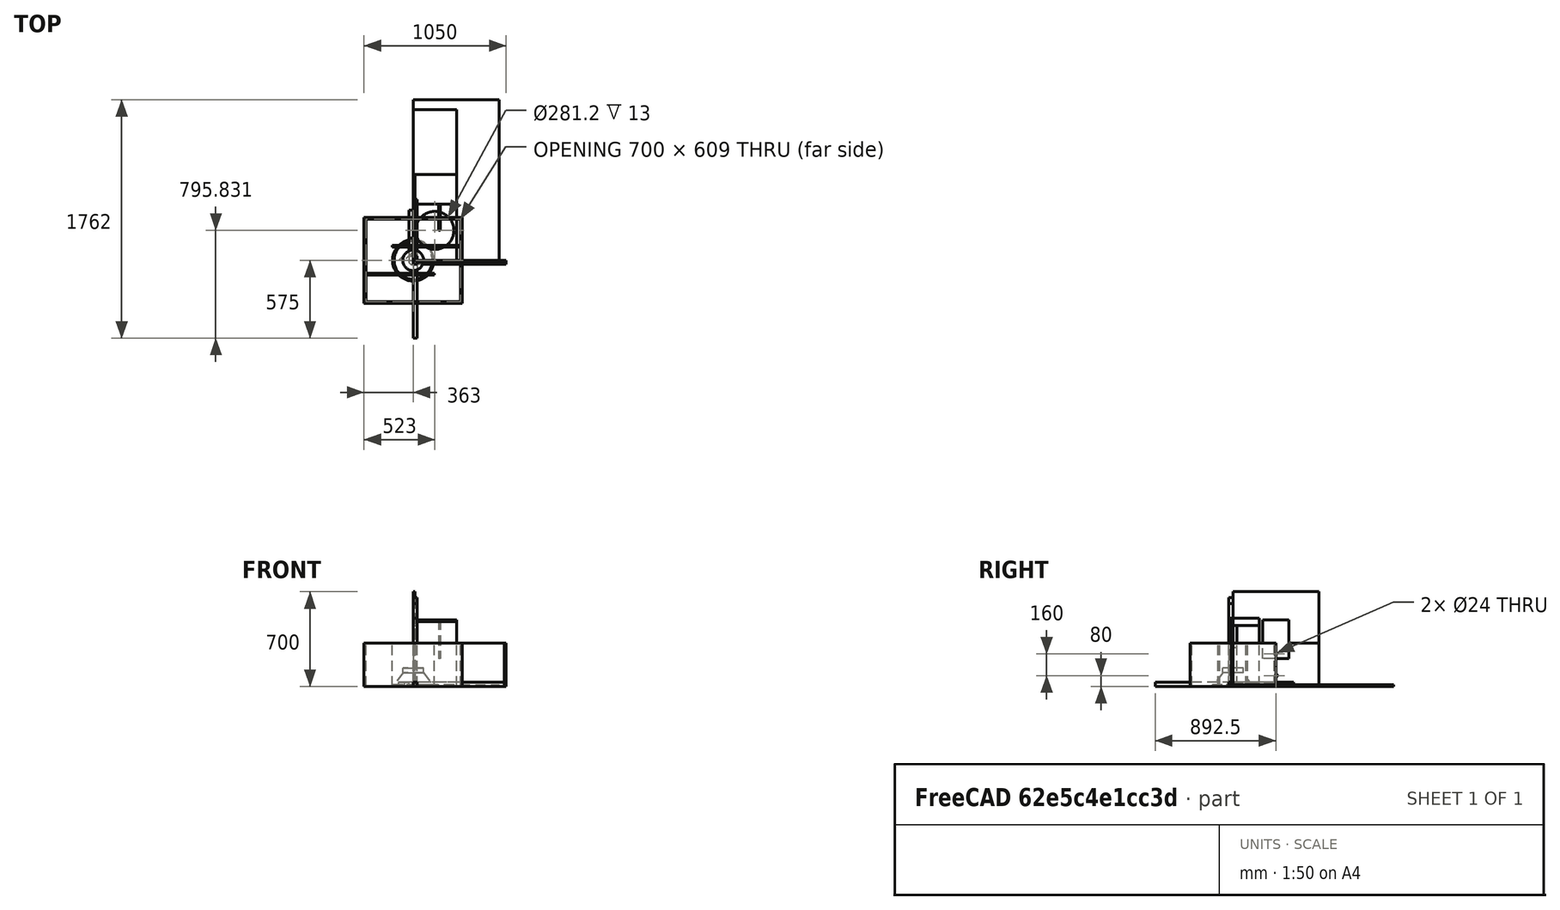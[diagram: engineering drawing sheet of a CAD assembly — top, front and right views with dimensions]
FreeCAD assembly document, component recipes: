
FREECAD ASSEMBLY — COMPONENT RECIPES ("gfold")

This assembly document has 41 components, labeled P0..P40 below (a component is one placed body or linked part). 41 of them carry a construction recipe — the FreeCAD feature program that regenerates the part from scratch, quoted from this document or its linked companion documents; the rest are supplied as boundary geometry only. No exploded tour is included for this assembly.
COMPONENT P0 — recipe-attached ("fin_support_1and2", modeled in this document).
Construction recipe (the document's own serialized feature program — sketch geometry with constraints, then the solid features built on it; lengths are millimeters unless a unit is written):

FEATURE [Sketcher::SketchObject] Sketch046
  ArcFitTolerance = 1e-06
  AttachmentSupport = -> [YZ_Plane037]
  FullyConstrained = true
  MakeInternals = false
  MapMode = 5
  Placement = pos=(0,0,0) rot=(0.57735,0.57735,0.57735;2.0944rad)
  expr: Constraints[10] = <<bdim>>.f12s_w
  expr: Constraints[9] = <<bdim>>.f12s_h
  sketch-geometry (4):
    g0: LineSegment StartX=0 StartY=0 StartZ=0 EndX=194.331 EndY=0 EndZ=0
    g1: LineSegment StartX=194.331 StartY=0 StartZ=0 EndX=194.331 EndY=285.337 EndZ=0
    g2: LineSegment StartX=194.331 StartY=285.337 StartZ=0 EndX=0 EndY=285.337 EndZ=0
    g3: LineSegment StartX=0 StartY=285.337 StartZ=0 EndX=0 EndY=0 EndZ=0
  constraints (11):
    c: Coincident(g0,g1)
    c: Coincident(g1,g2)
    c: Coincident(g2,g3)
    c: Coincident(g3,g0)
    c: Horizontal(g0)
    c: Horizontal(g2)
    c: Vertical(g1)
    c: Vertical(g3)
    c: Coincident(g0,g-1)
    c: DistanceX(g2,g2) = 194.331
    c: DistanceY(g1,g1) = 285.337
FEATURE [PartDesign::Pad] Pad034
  Direction = (1,0,0)
  Length = 13
  Length2 = 10
  Placement = pos=(0,0,0) rot=(1,1,1;2.0944rad)
  Profile = -> Sketch046
  ReferenceAxis = -> Sketch046 [N_Axis]
  Suppressed = false
  Type = 0
  expr: Length = <<bdim>>.f12s_t
FEATURE [PartDesign::Body] Body036  label="fin_support_1and2"
  AllowCompound = false
  Group = -> [Sketch046,Pad034]
  Origin = -> Origin037
  Placement = pos=(201,220.337,492.669) rot=(0,1,0;3.14159rad)
  Tip = -> Pad034
COMPONENT P1 — recipe-attached ("12lfa_driver001", modeled in this document).
Construction recipe (the document's own serialized feature program — sketch geometry with constraints, then the solid features built on it; lengths are millimeters unless a unit is written):

FEATURE [Sketcher::SketchObject] Sketch019
  ArcFitTolerance = 1e-06
  AttachmentSupport = -> [YZ_Plane009]
  FullyConstrained = true
  MakeInternals = false
  MapMode = 5
  Placement = pos=(0,0,0) rot=(0.57735,0.57735,0.57735;2.0944rad)
  expr: Constraints[18] = <<bdim>>.dr_d
  expr: Constraints[19] = <<bdim>>.dr_tdiam / 2
  expr: Constraints[20] = 6.4 mm
  expr: Constraints[22] = <<bdim>>.baffle_diameter / 2
  expr: Constraints[23] = <<bdim>>.dr_tdiam / 4
  expr: Constraints[24] = <<bdim>>.dr_d / 4
  expr: Constraints[25] = <<bdim>>.dr_d / 4
  sketch-geometry (9):
    g0: ArcOfCircle CenterX=0 CenterY=207.3 CenterZ=0 NormalX=0 NormalY=0 NormalZ=1 AngleXU=0 Radius=207.3 StartAngle=4.71239 EndAngle=4.87702
    g1: LineSegment StartX=33.975 StartY=2.80308 StartZ=0 EndX=146.4 EndY=0 EndZ=0
    g2: LineSegment StartX=146.4 StartY=0 StartZ=0 EndX=152.8 EndY=0 EndZ=0
    g3: LineSegment StartX=152.8 StartY=0 StartZ=0 EndX=152.8 EndY=12.2 EndZ=0
    g4: LineSegment StartX=152.8 StartY=12.2 StartZ=0 EndX=140.6 EndY=12.2 EndZ=0
    g5: LineSegment StartX=140.6 StartY=12.2 StartZ=0 EndX=76.4 EndY=101.925 EndZ=0
    g6: LineSegment StartX=76.4 StartY=101.925 StartZ=0 EndX=76.4 EndY=135.9 EndZ=0
    g7: LineSegment StartX=76.4 StartY=135.9 StartZ=0 EndX=0 EndY=135.9 EndZ=0
    g8: LineSegment StartX=0 StartY=135.9 StartZ=0 EndX=-3.81e-14 EndY=0 EndZ=0
  constraints (27):
    c: Coincident(g0,g-1)
    c: PointOnObject(g0,g-2)
    c: Coincident(g1,g0)
    c: PointOnObject(g1,g-1)
    c: Coincident(g1,g2)
    c: PointOnObject(g2,g-1)
    c: Coincident(g2,g3)
    c: Vertical(g3)
    c: Coincident(g3,g4)
    c: Horizontal(g4)
    c: Coincident(g4,g5)
    c: Coincident(g5,g6)
    c: Vertical(g6)
    c: Coincident(g6,g7)
    c: PointOnObject(g7,g-2)
    c: Horizontal(g7)
    c: Coincident(g7,g8)
    c: Coincident(g8,g0)
    c: DistanceY(g8,g8) = 135.9
    c: DistanceX(g0,g2) = 152.8
    c: DistanceX(g2,g2) = 6.4
    c: Radius(g0) = 207.3
    c: DistanceX(g0,g4) = 140.6
    c: DistanceX(g7,g7) = 76.4
    c: DistanceY(g6,g6) = 33.975
    c: DistanceX(g0,g0) = 33.975
    c: Equal(g3,g4)
FEATURE [PartDesign::Revolution] Revolution
  Angle = 360
  Angle2 = 60
  Axis = (0,0,1)
  Base = (0,0,0)
  Placement = pos=(0,0,0) rot=(1,1,1;2.0944rad)
  Profile = -> Sketch019
  ReferenceAxis = -> Sketch019 [V_Axis]
  Reversed = true
  Suppressed = false
  Type = 0
FEATURE [PartDesign::Body] Body008  label="12lfa_driver"
  AllowCompound = false
  Group = -> [Sketch019,Revolution]
  Origin = -> Origin009
  Tip = -> Revolution
COMPONENT P2 — recipe-attached ("back_panel001", modeled in this document).
Construction recipe (the document's own serialized feature program — sketch geometry with constraints, then the solid features built on it; lengths are millimeters unless a unit is written):

FEATURE [Sketcher::SketchObject] Sketch014
  ArcFitTolerance = 1e-06
  AttachmentSupport = -> [YZ_Plane004]
  FullyConstrained = true
  MakeInternals = false
  MapMode = 5
  Placement = pos=(0,0,0) rot=(0.57735,0.57735,0.57735;2.0944rad)
  expr: Constraints[10] = <<bdim>>.bp_w
  expr: Constraints[25] = <<bdim>>.bp_h * 0.25
  expr: Constraints[26] = <<bdim>>.spkon_bl
  expr: Constraints[28] = <<bdim>>.spkon_cd
  expr: Constraints[29] = <<bdim>>.bp_w / 2
  expr: Constraints[31] = <<bdim>>.bp_h * 0.25
  expr: Constraints[32] = <<bdim>>.bp_w / 2
  expr: Constraints[9] = <<bdim>>.bp_h
  sketch-geometry (13):
    g0: LineSegment StartX=0 StartY=0 StartZ=0 EndX=635 EndY=0 EndZ=0
    g1: LineSegment StartX=635 StartY=0 StartZ=0 EndX=635 EndY=320 EndZ=0
    g2: LineSegment StartX=635 StartY=320 StartZ=0 EndX=0 EndY=320 EndZ=0
    g3: LineSegment StartX=0 StartY=320 StartZ=0 EndX=0 EndY=0 EndZ=0
    g4: LineSegment [constr] StartX=332.1 StartY=254.6 StartZ=0 EndX=332.1 EndY=225.4 EndZ=0
    g5: LineSegment [constr] StartX=332.1 StartY=225.4 StartZ=0 EndX=302.9 EndY=225.4 EndZ=0
    g6: LineSegment [constr] StartX=302.9 StartY=225.4 StartZ=0 EndX=302.9 EndY=254.6 EndZ=0
    g7: LineSegment [constr] StartX=302.9 StartY=254.6 StartZ=0 EndX=332.1 EndY=254.6 EndZ=0
    g8: LineSegment [constr] StartX=332.1 StartY=225.4 StartZ=0 EndX=302.9 EndY=254.6 EndZ=0
    g9: LineSegment [constr] StartX=302.9 StartY=225.4 StartZ=0 EndX=332.1 EndY=254.6 EndZ=0
    g10: GeomPoint [constr] X=317.5 Y=240 Z=0
    g11: Circle CenterX=317.5 CenterY=240 CenterZ=0 NormalX=0 NormalY=0 NormalZ=1 AngleXU=0 Radius=12
    g12: Circle CenterX=317.5 CenterY=80 CenterZ=0 NormalX=0 NormalY=0 NormalZ=1 AngleXU=0 Radius=12
  constraints (33):
    c: Coincident(g0,g1)
    c: Coincident(g1,g2)
    c: Coincident(g2,g3)
    c: Coincident(g3,g0)
    c: Horizontal(g0)
    c: Horizontal(g2)
    c: Vertical(g1)
    c: Vertical(g3)
    c: Coincident(g0,g-1)
    c: DistanceY(g3,g3) = 320
    c: DistanceX(g0,g0) = 635
    c: Coincident(g4,g5)
    c: Coincident(g5,g6)
    c: Coincident(g6,g7)
    c: Coincident(g7,g4)
    c: Vertical(g4)
    c: Vertical(g6)
    c: Horizontal(g5)
    c: Horizontal(g7)
    c: Equal(g5,g4)
    c: Coincident(g8,g4)
    c: Coincident(g8,g6)
    c: Coincident(g9,g5)
    c: Coincident(g9,g4)
    c: Symmetric(g8,g8,g10)
    c: DistanceY(g10,g2) = 80
    c: DistanceY(g6,g6) = 29.2
    c: Coincident(g11,g10)
    c: Diameter(g11) = 24
    c: DistanceX(g2,g10) = 317.5
    c: Equal(g12,g11)
    c: DistanceY(g0,g12) = 80
    c: DistanceX(g0,g12) = 317.5
FEATURE [PartDesign::Pad] Pad003
  Direction = (1,0,0)
  Length = 13
  Length2 = 10
  Placement = pos=(0,0,0) rot=(1,1,1;2.0944rad)
  Profile = -> Sketch014
  ReferenceAxis = -> Sketch014 [N_Axis]
  Suppressed = false
  Type = 0
  expr: Length = <<bdim>>.bp_t
FEATURE [PartDesign::Body] Body003  label="back_panel"
  AllowCompound = false
  Group = -> [Sketch014,Pad003]
  Origin = -> Origin004
  Tip = -> Pad003
COMPONENT P3 — recipe-attached ("bottom_panel001", modeled in this document).
Construction recipe (the document's own serialized feature program — sketch geometry with constraints, then the solid features built on it; lengths are millimeters unless a unit is written):

FEATURE [Sketcher::SketchObject] Sketch017
  ArcFitTolerance = 1e-06
  AttachmentSupport = -> [YZ_Plane007]
  FullyConstrained = true
  MakeInternals = false
  MapMode = 5
  Placement = pos=(0,0,0) rot=(0.57735,0.57735,0.57735;2.0944rad)
  expr: Constraints[10] = <<bdim>>.tp_h
  expr: Constraints[9] = <<bdim>>.tp_w
  sketch-geometry (4):
    g0: LineSegment StartX=0 StartY=0 StartZ=0 EndX=635 EndY=0 EndZ=0
    g1: LineSegment StartX=635 StartY=0 StartZ=0 EndX=635 EndY=700 EndZ=0
    g2: LineSegment StartX=635 StartY=700 StartZ=0 EndX=0 EndY=700 EndZ=0
    g3: LineSegment StartX=0 StartY=700 StartZ=0 EndX=0 EndY=0 EndZ=0
  constraints (11):
    c: Coincident(g0,g1)
    c: Coincident(g1,g2)
    c: Coincident(g2,g3)
    c: Coincident(g3,g0)
    c: Horizontal(g0)
    c: Horizontal(g2)
    c: Vertical(g1)
    c: Vertical(g3)
    c: Coincident(g0,g-1)
    c: DistanceX(g0,g0) = 635
    c: DistanceY(g3,g3) = 700
FEATURE [PartDesign::Pad] Pad006
  Direction = (1,0,0)
  Length = 13
  Length2 = 10
  Placement = pos=(0,0,0) rot=(1,1,1;2.0944rad)
  Profile = -> Sketch017
  ReferenceAxis = -> Sketch017 [N_Axis]
  Suppressed = false
  Type = 0
  expr: Length = <<bdim>>.tp_t
FEATURE [PartDesign::Body] Body006  label="bottom_panel"
  AllowCompound = false
  Group = -> [Sketch017,Pad006]
  Origin = -> Origin007
  Tip = -> Pad006
COMPONENT P4 — recipe-attached ("brace_bar_back_panel_b", modeled in this document).
Construction recipe (the document's own serialized feature program — sketch geometry with constraints, then the solid features built on it; lengths are millimeters unless a unit is written):

FEATURE [Sketcher::SketchObject] Sketch037
  ArcFitTolerance = 1e-06
  AttachmentSupport = -> [XY_Plane027]
  FullyConstrained = true
  MakeInternals = false
  MapMode = 5
  expr: Constraints[10] = <<bdim>>.bbbp1_w
  expr: Constraints[9] = <<bdim>>.bbbp1_t
  sketch-geometry (4):
    g0: LineSegment StartX=0 StartY=0 StartZ=0 EndX=0 EndY=371.669 EndZ=0
    g1: LineSegment StartX=0 StartY=371.669 StartZ=0 EndX=-30 EndY=371.669 EndZ=0
    g2: LineSegment StartX=-30 StartY=371.669 StartZ=0 EndX=-30 EndY=0 EndZ=0
    g3: LineSegment StartX=-30 StartY=0 StartZ=0 EndX=0 EndY=0 EndZ=0
  constraints (11):
    c: Coincident(g0,g1)
    c: Coincident(g1,g2)
    c: Coincident(g2,g3)
    c: Coincident(g3,g0)
    c: Vertical(g0)
    c: Vertical(g2)
    c: Horizontal(g1)
    c: Horizontal(g3)
    c: Coincident(g0,g-1)
    c: DistanceX(g1,g1) = 30
    c: DistanceY(g2,g2) = 371.669
FEATURE [PartDesign::Pad] Pad025
  Direction = (0,0,1)
  Length = 30
  Length2 = 10
  Profile = -> Sketch037
  ReferenceAxis = -> Sketch037 [N_Axis]
  Suppressed = false
  Type = 0
  expr: Length = <<bdim>>.bbbp1_t
FEATURE [PartDesign::Body] Body026  label="brace_bar_back_panel_2"
  AllowCompound = false
  Group = -> [Sketch037,Pad025]
  Origin = -> Origin027
  Tip = -> Pad025
COMPONENT P5 — recipe-attached ("brace_bar_back_panel_c", modeled in this document).
Construction recipe (the document's own serialized feature program — sketch geometry with constraints, then the solid features built on it; lengths are millimeters unless a unit is written):

FEATURE [Sketcher::SketchObject] Sketch036
  ArcFitTolerance = 1e-06
  AttachmentSupport = -> [XY_Plane026]
  FullyConstrained = true
  MakeInternals = false
  MapMode = 5
  expr: Constraints[10] = <<bdim>>.bbbp2_w
  expr: Constraints[9] = <<bdim>>.bbbp2_t
  sketch-geometry (4):
    g0: LineSegment StartX=0 StartY=0 StartZ=0 EndX=0 EndY=164.331 EndZ=0
    g1: LineSegment StartX=0 StartY=164.331 StartZ=0 EndX=-30 EndY=164.331 EndZ=0
    g2: LineSegment StartX=-30 StartY=164.331 StartZ=0 EndX=-30 EndY=0 EndZ=0
    g3: LineSegment StartX=-30 StartY=0 StartZ=0 EndX=0 EndY=0 EndZ=0
  constraints (11):
    c: Coincident(g0,g1)
    c: Coincident(g1,g2)
    c: Coincident(g2,g3)
    c: Coincident(g3,g0)
    c: Vertical(g0)
    c: Vertical(g2)
    c: Horizontal(g1)
    c: Horizontal(g3)
    c: Coincident(g0,g-1)
    c: DistanceX(g1,g1) = 30
    c: DistanceY(g2,g2) = 164.331
FEATURE [PartDesign::Pad] Pad024
  Direction = (0,0,1)
  Length = 30
  Length2 = 10
  Profile = -> Sketch036
  ReferenceAxis = -> Sketch036 [N_Axis]
  Suppressed = false
  Type = 0
  expr: Length = <<bdim>>.bbbp1_t
FEATURE [PartDesign::Body] Body025  label="brace_bar_back_panel_1"
  AllowCompound = false
  Group = -> [Sketch036,Pad024]
  Origin = -> Origin026
  Tip = -> Pad024
COMPONENT P6 — same part as P4; its construction recipe is shown at P4.
COMPONENT P7 — same part as P5; its construction recipe is shown at P5.
COMPONENT P8 — same part as P4; its construction recipe is shown at P4.
COMPONENT P9 — recipe-attached ("brace bar fin 2 a", modeled in this document).
Construction recipe (the document's own serialized feature program — sketch geometry with constraints, then the solid features built on it; lengths are millimeters unless a unit is written):

FEATURE [Sketcher::SketchObject] Sketch034
  ArcFitTolerance = 1e-06
  AttachmentSupport = -> [YZ_Plane024]
  FullyConstrained = true
  MakeInternals = false
  MapMode = 5
  Placement = pos=(0,0,0) rot=(0.57735,0.57735,0.57735;2.0944rad)
  expr: Constraints[10] = <<bdim>>.bbf2_w
  expr: Constraints[9] = <<bdim>>.bbf2_h
  sketch-geometry (4):
    g0: LineSegment StartX=0 StartY=0 StartZ=0 EndX=30 EndY=0 EndZ=0
    g1: LineSegment StartX=30 StartY=0 StartZ=0 EndX=30 EndY=449.669 EndZ=0
    g2: LineSegment StartX=30 StartY=449.669 StartZ=0 EndX=0 EndY=449.669 EndZ=0
    g3: LineSegment StartX=0 StartY=449.669 StartZ=0 EndX=0 EndY=0 EndZ=0
  constraints (11):
    c: Coincident(g0,g1)
    c: Coincident(g1,g2)
    c: Coincident(g2,g3)
    c: Coincident(g3,g0)
    c: Horizontal(g0)
    c: Horizontal(g2)
    c: Vertical(g1)
    c: Vertical(g3)
    c: Coincident(g0,g-1)
    c: DistanceX(g2,g2) = 30
    c: DistanceY(g1,g1) = 449.669
FEATURE [PartDesign::Pad] Pad022
  Direction = (1,0,0)
  Length = 30
  Length2 = 10
  Placement = pos=(0,0,0) rot=(1,1,1;2.0944rad)
  Profile = -> Sketch034
  ReferenceAxis = -> Sketch034 [N_Axis]
  Suppressed = false
  Type = 0
  expr: Length = <<bdim>>.bbf2_t
FEATURE [PartDesign::Body] Body023  label="brace bar fin 2"
  AllowCompound = false
  Group = -> [Sketch034,Pad022]
  Origin = -> Origin024
  Tip = -> Pad022
COMPONENT P10 — recipe-attached ("brace bar fin 1 a", modeled in this document).
Construction recipe (the document's own serialized feature program — sketch geometry with constraints, then the solid features built on it; lengths are millimeters unless a unit is written):

FEATURE [Sketcher::SketchObject] Sketch035
  ArcFitTolerance = 1e-06
  AttachmentSupport = -> [YZ_Plane025]
  FullyConstrained = true
  MakeInternals = false
  MapMode = 5
  Placement = pos=(0,0,0) rot=(0.57735,0.57735,0.57735;2.0944rad)
  expr: Constraints[10] = <<bdim>>.bbf1_w
  expr: Constraints[9] = <<bdim>>.bbf2_h
  sketch-geometry (4):
    g0: LineSegment StartX=0 StartY=0 StartZ=0 EndX=30 EndY=0 EndZ=0
    g1: LineSegment StartX=30 StartY=0 StartZ=0 EndX=30 EndY=449.669 EndZ=0
    g2: LineSegment StartX=30 StartY=449.669 StartZ=0 EndX=0 EndY=449.669 EndZ=0
    g3: LineSegment StartX=0 StartY=449.669 StartZ=0 EndX=0 EndY=0 EndZ=0
  constraints (11):
    c: Coincident(g0,g1)
    c: Coincident(g1,g2)
    c: Coincident(g2,g3)
    c: Coincident(g3,g0)
    c: Horizontal(g0)
    c: Horizontal(g2)
    c: Vertical(g1)
    c: Vertical(g3)
    c: Coincident(g0,g-1)
    c: DistanceX(g2,g2) = 30
    c: DistanceY(g1,g1) = 449.669
FEATURE [PartDesign::Pad] Pad023
  Direction = (1,0,0)
  Length = 30
  Length2 = 10
  Placement = pos=(0,0,0) rot=(1,1,1;2.0944rad)
  Profile = -> Sketch035
  ReferenceAxis = -> Sketch035 [N_Axis]
  Suppressed = false
  Type = 0
  expr: Length = <<bdim>>.bbf2_t
FEATURE [PartDesign::Body] Body024  label="brace bar fin 1"
  AllowCompound = false
  Group = -> [Sketch035,Pad023]
  Origin = -> Origin025
  Tip = -> Pad023
COMPONENT P11 — same part as P10; its construction recipe is shown at P10.
COMPONENT P12 — same part as P9; its construction recipe is shown at P9.
COMPONENT P13 — recipe-attached ("driver_brace_bar_a", modeled in this document).
Construction recipe (the document's own serialized feature program — sketch geometry with constraints, then the solid features built on it; lengths are millimeters unless a unit is written):

FEATURE [Sketcher::SketchObject] Sketch038
  ArcFitTolerance = 1e-06
  AttachmentSupport = -> [XY_Plane029]
  FullyConstrained = true
  MakeInternals = false
  MapMode = 5
  expr: Constraints[12] = <<bdim>>.dbb_h
  expr: Constraints[13] = <<bdim>>.dbb_w
  sketch-geometry (5):
    g0: LineSegment StartX=0 StartY=106.066 StartZ=0 EndX=0 EndY=63.6396 EndZ=0
    g1: LineSegment StartX=0 StartY=63.6396 StartZ=0 EndX=-63.6396 EndY=0 EndZ=0
    g2: LineSegment StartX=-63.6396 StartY=0 StartZ=0 EndX=-106.066 EndY=0 EndZ=0
    g3: LineSegment StartX=-106.066 StartY=0 StartZ=0 EndX=0 EndY=106.066 EndZ=0
    g4: LineSegment [constr] StartX=-84.8528 StartY=21.2132 StartZ=0 EndX=-63.6396 EndY=0 EndZ=0
  constraints (15):
    c: PointOnObject(g0,g-2)
    c: PointOnObject(g0,g-2)
    c: Coincident(g0,g1)
    c: PointOnObject(g1,g-1)
    c: Coincident(g1,g2)
    c: PointOnObject(g2,g-1)
    c: Coincident(g2,g3)
    c: Coincident(g3,g0)
    c: Equal(g0,g2)
    c: Parallel(g3,g1)
    c: PointOnObject(g4,g3)
    c: Perpendicular(g3,g4)
    c: Distance(g4) = 30
    c: Distance(g3) = 150
    c: Coincident(g4,g1)
FEATURE [PartDesign::Pad] Pad027
  Direction = (0,0,1)
  Length = 30
  Length2 = 10
  Profile = -> Sketch038
  ReferenceAxis = -> Sketch038 [N_Axis]
  Suppressed = false
  Type = 0
  expr: Length = <<bdim>>.dbb_t
FEATURE [PartDesign::Body] Body028  label="driver_brace_bar"
  AllowCompound = false
  Group = -> [Sketch038,Pad027]
  Origin = -> Origin029
  Tip = -> Pad027
COMPONENT P14 — same part as P13; its construction recipe is shown at P13.
COMPONENT P15 — recipe-attached ("fin_1", modeled in this document).
Construction recipe (the document's own serialized feature program — sketch geometry with constraints, then the solid features built on it; lengths are millimeters unless a unit is written):

FEATURE [Sketcher::SketchObject] Sketch030
  ArcFitTolerance = 1e-06
  AttachmentSupport = -> [XZ_Plane020]
  FullyConstrained = true
  MakeInternals = false
  MapMode = 5
  Placement = pos=(0,0,0) rot=(1,0,0;1.5708rad)
  expr: Constraints[10] = <<bdim>>.f1_h
  expr: Constraints[9] = <<bdim>>.f1_w
  sketch-geometry (4):
    g0: LineSegment StartX=0 StartY=0 StartZ=0 EndX=320 EndY=0 EndZ=0
    g1: LineSegment StartX=320 StartY=0 StartZ=0 EndX=320 EndY=479.669 EndZ=0
    g2: LineSegment StartX=320 StartY=479.669 StartZ=0 EndX=0 EndY=479.669 EndZ=0
    g3: LineSegment StartX=0 StartY=479.669 StartZ=0 EndX=0 EndY=0 EndZ=0
  constraints (11):
    c: Coincident(g0,g1)
    c: Coincident(g1,g2)
    c: Coincident(g2,g3)
    c: Coincident(g3,g0)
    c: Horizontal(g0)
    c: Horizontal(g2)
    c: Vertical(g1)
    c: Vertical(g3)
    c: Coincident(g0,g-1)
    c: DistanceY(g1,g1) = 479.669
    c: DistanceX(g0,g0) = 320
FEATURE [PartDesign::Pad] Pad018
  Direction = (0,-1,2e-16)
  Length = 13
  Length2 = 10
  Placement = pos=(0,0,0) rot=(1,0,0;1.5708rad)
  Profile = -> Sketch030
  ReferenceAxis = -> Sketch030 [N_Axis]
  Suppressed = false
  Type = 0
  expr: Length = <<bdim>>.f1_t
FEATURE [PartDesign::Body] Body019  label="fin_1_model"
  AllowCompound = false
  Group = -> [Sketch030,Pad018]
  Origin = -> Origin020
  Tip = -> Pad018
COMPONENT P16 — recipe-attached ("fin 1 support001", modeled in this document).
Construction recipe (the document's own serialized feature program — sketch geometry with constraints, then the solid features built on it; lengths are millimeters unless a unit is written):

FEATURE [Sketcher::SketchObject] Sketch042
  ArcFitTolerance = 1e-06
  AttachmentSupport = -> [YZ_Plane033]
  FullyConstrained = true
  MakeInternals = false
  MapMode = 5
  Placement = pos=(0,0,0) rot=(0.57735,0.57735,0.57735;2.0944rad)
  expr: Constraints[10] = <<bdim>>.f2s_w
  expr: Constraints[9] = <<bdim>>.f2s_h
  sketch-geometry (4):
    g0: LineSegment StartX=0 StartY=0 StartZ=0 EndX=194.331 EndY=0 EndZ=0
    g1: LineSegment StartX=194.331 StartY=0 StartZ=0 EndX=194.331 EndY=505.669 EndZ=0
    g2: LineSegment StartX=194.331 StartY=505.669 StartZ=0 EndX=0 EndY=505.669 EndZ=0
    g3: LineSegment StartX=0 StartY=505.669 StartZ=0 EndX=0 EndY=0 EndZ=0
  constraints (11):
    c: Coincident(g0,g1)
    c: Coincident(g1,g2)
    c: Coincident(g2,g3)
    c: Coincident(g3,g0)
    c: Horizontal(g0)
    c: Horizontal(g2)
    c: Vertical(g1)
    c: Vertical(g3)
    c: Coincident(g0,g-1)
    c: DistanceX(g2,g2) = 194.331
    c: DistanceY(g3,g3) = 505.669
FEATURE [PartDesign::Pad] Pad030
  Direction = (1,0,0)
  Length = 13
  Length2 = 10
  Placement = pos=(0,0,0) rot=(1,1,1;2.0944rad)
  Profile = -> Sketch042
  ReferenceAxis = -> Sketch042 [N_Axis]
  Suppressed = false
  Type = 0
  expr: Length = <<bdim>>.f2s_t
FEATURE [PartDesign::Body] Body032  label="fin 2 support"
  AllowCompound = false
  Group = -> [Sketch042,Pad030]
  Origin = -> Origin033
  Tip = -> Pad030
COMPONENT P17 — recipe-attached ("fin 1 support002", modeled in this document).
Construction recipe (the document's own serialized feature program — sketch geometry with constraints, then the solid features built on it; lengths are millimeters unless a unit is written):

FEATURE [Sketcher::SketchObject] Sketch043
  ArcFitTolerance = 1e-06
  AttachmentSupport = -> [YZ_Plane034]
  FullyConstrained = true
  MakeInternals = false
  MapMode = 5
  Placement = pos=(0,0,0) rot=(0.57735,0.57735,0.57735;2.0944rad)
  expr: Constraints[10] = <<bdim>>.f1s_w
  expr: Constraints[9] = <<bdim>>.f1s_h
  sketch-geometry (4):
    g0: LineSegment StartX=0 StartY=0 StartZ=0 EndX=194.331 EndY=0 EndZ=0
    g1: LineSegment StartX=194.331 StartY=0 StartZ=0 EndX=194.331 EndY=449.669 EndZ=0
    g2: LineSegment StartX=194.331 StartY=449.669 StartZ=0 EndX=0 EndY=449.669 EndZ=0
    g3: LineSegment StartX=0 StartY=449.669 StartZ=0 EndX=0 EndY=0 EndZ=0
  constraints (11):
    c: Coincident(g0,g1)
    c: Coincident(g1,g2)
    c: Coincident(g2,g3)
    c: Coincident(g3,g0)
    c: Horizontal(g0)
    c: Horizontal(g2)
    c: Vertical(g1)
    c: Vertical(g3)
    c: Coincident(g0,g-1)
    c: DistanceX(g2,g2) = 194.331
    c: DistanceY(g3,g3) = 449.669
FEATURE [PartDesign::Pad] Pad031
  Direction = (1,0,0)
  Length = 13
  Length2 = 10
  Placement = pos=(0,0,0) rot=(1,1,1;2.0944rad)
  Profile = -> Sketch043
  ReferenceAxis = -> Sketch043 [N_Axis]
  Suppressed = false
  Type = 0
  expr: Length = <<bdim>>.f1s_t
FEATURE [PartDesign::Body] Body033  label="fin 1 support"
  AllowCompound = false
  Group = -> [Sketch043,Pad031]
  Origin = -> Origin034
  Tip = -> Pad031
COMPONENT P18 — recipe-attached ("fin_2", modeled in this document).
Construction recipe (the document's own serialized feature program — sketch geometry with constraints, then the solid features built on it; lengths are millimeters unless a unit is written):

FEATURE [Sketcher::SketchObject] Sketch031
  ArcFitTolerance = 1e-06
  AttachmentSupport = -> [XZ_Plane021]
  FullyConstrained = true
  MakeInternals = false
  MapMode = 5
  Placement = pos=(0,0,0) rot=(1,0,0;1.5708rad)
  expr: Constraints[10] = <<bdim>>.f2_h
  expr: Constraints[9] = <<bdim>>.f2_w
  sketch-geometry (4):
    g0: LineSegment StartX=0 StartY=0 StartZ=0 EndX=320 EndY=0 EndZ=0
    g1: LineSegment StartX=320 StartY=0 StartZ=0 EndX=320 EndY=492.669 EndZ=0
    g2: LineSegment StartX=320 StartY=492.669 StartZ=0 EndX=0 EndY=492.669 EndZ=0
    g3: LineSegment StartX=0 StartY=492.669 StartZ=0 EndX=0 EndY=0 EndZ=0
  constraints (11):
    c: Coincident(g0,g1)
    c: Coincident(g1,g2)
    c: Coincident(g2,g3)
    c: Coincident(g3,g0)
    c: Horizontal(g0)
    c: Horizontal(g2)
    c: Vertical(g1)
    c: Vertical(g3)
    c: Coincident(g0,g-1)
    c: DistanceY(g1,g1) = 492.669
    c: DistanceX(g0,g0) = 320
FEATURE [PartDesign::Pad] Pad019
  Direction = (0,-1,2e-16)
  Length = 13
  Length2 = 10
  Placement = pos=(0,0,0) rot=(1,0,0;1.5708rad)
  Profile = -> Sketch031
  ReferenceAxis = -> Sketch031 [N_Axis]
  Suppressed = false
  Type = 0
  expr: Length = <<bdim>>.f2_t
FEATURE [PartDesign::Body] Body020  label="fin_2_model"
  AllowCompound = false
  Group = -> [Sketch031,Pad019]
  Origin = -> Origin021
  Tip = -> Pad019
COMPONENT P19 — recipe-attached ("front_panel_bar_b", modeled in this document).
Construction recipe (the document's own serialized feature program — sketch geometry with constraints, then the solid features built on it; lengths are millimeters unless a unit is written):

FEATURE [Sketcher::SketchObject] Sketch033
  ArcFitTolerance = 1e-06
  AttachmentSupport = -> [XY_Plane023]
  FullyConstrained = true
  MakeInternals = false
  MapMode = 5
  expr: Constraints[13] = <<bdim>>.fpb_h
  expr: Constraints[15] = (<<bdim>>.baffle_diameter + <<bdim>>.dr_tdiam) / 4
  expr: Constraints[16] = <<bdim>>.fp_h / 2
  expr: Constraints[17] = <<dims>>.width1 + <<bdim>>.sp_thick * 0.5 + <<dims>>.driver_offset - <<bdim>>.bar_side_size - <<bdim>>.sp_thick
  expr: Constraints[6] = <<bdim>>.fpb_t
  sketch-geometry (6):
    g0: LineSegment StartX=0 StartY=0 StartZ=0 EndX=30 EndY=0 EndZ=0
    g1: LineSegment StartX=30 StartY=371.663 StartZ=0 EndX=0 EndY=371.663 EndZ=0
    g2: LineSegment StartX=0 StartY=371.663 StartZ=0 EndX=0 EndY=0 EndZ=0
    g3: LineSegment StartX=30 StartY=371.663 StartZ=0 EndX=30 EndY=261.809 EndZ=0
    g4: LineSegment StartX=30 StartY=0 StartZ=0 EndX=30 EndY=125.854 EndZ=0
    g5: ArcOfCircle CenterX=160 CenterY=193.831 CenterZ=0 NormalX=0 NormalY=0 NormalZ=1 AngleXU=0 Radius=146.7 StartAngle=2.65979 EndAngle=3.62339
  constraints (18):
    c: Coincident(g1,g2)
    c: Coincident(g2,g0)
    c: Horizontal(g0)
    c: Horizontal(g1)
    c: Vertical(g2)
    c: Coincident(g0,g-1)
    c: DistanceX(g1,g1) = 30
    c: Coincident(g3,g1)
    c: Vertical(g3)
    c: Coincident(g4,g0)
    c: Vertical(g4)
    c: Coincident(g5,g3)
    c: Coincident(g5,g4)
    c: DistanceY(g2,g2) = 371.663
    c: Equal(g1,g0)
    c: Radius(g5) = 146.7
    c: DistanceX(g0,g5) = 160
    c: DistanceY(g5,g1) = 177.831
FEATURE [PartDesign::Pad] Pad021
  Direction = (0,0,1)
  Length = 30
  Length2 = 10
  Profile = -> Sketch033
  ReferenceAxis = -> Sketch033 [N_Axis]
  Suppressed = false
  Type = 0
  expr: Length = <<bdim>>.bar_side_size
FEATURE [PartDesign::Body] Body022  label="fp_bar_1"
  AllowCompound = false
  Group = -> [Sketch033,Pad021]
  Origin = -> Origin023
  Tip = -> Pad021
COMPONENT P20 — same part as P19; its construction recipe is shown at P19.
COMPONENT P21 — recipe-attached ("front_panel001", modeled in this document).
Construction recipe (the document's own serialized feature program — sketch geometry with constraints, then the solid features built on it; lengths are millimeters unless a unit is written):

FEATURE [Sketcher::SketchObject] Sketch032
  ArcFitTolerance = 1e-06
  AttachmentSupport = -> [XY_Plane022]
  FullyConstrained = true
  MakeInternals = false
  MapMode = 5
  expr: Constraints[10] = <<bdim>>.fp_w
  expr: Constraints[18] = <<bdim>>.baffle_diameter
  expr: Constraints[19] = <<dims>>.width1 + <<bdim>>.sp_thick * 0.5 + <<dims>>.driver_offset
  expr: Constraints[9] = <<bdim>>.fp_h
  sketch-geometry (7):
    g0: LineSegment StartX=0 StartY=0 StartZ=0 EndX=320 EndY=0 EndZ=0
    g1: LineSegment StartX=320 StartY=0 StartZ=0 EndX=320 EndY=414.663 EndZ=0
    g2: LineSegment StartX=320 StartY=414.663 StartZ=0 EndX=0 EndY=414.663 EndZ=0
    g3: LineSegment StartX=0 StartY=414.663 StartZ=0 EndX=0 EndY=0 EndZ=0
    g4: Circle CenterX=160 CenterY=220.831 CenterZ=0 NormalX=0 NormalY=0 NormalZ=1 AngleXU=0 Radius=140.6
    g5: LineSegment [constr] StartX=0 StartY=220.831 StartZ=0 EndX=160 EndY=220.831 EndZ=0
    g6: LineSegment [constr] StartX=160 StartY=220.831 StartZ=0 EndX=320 EndY=220.831 EndZ=0
  constraints (20):
    c: Coincident(g0,g1)
    c: Coincident(g1,g2)
    c: Coincident(g2,g3)
    c: Coincident(g3,g0)
    c: Horizontal(g0)
    c: Horizontal(g2)
    c: Vertical(g1)
    c: Vertical(g3)
    c: Coincident(g0,g-1)
    c: DistanceX(g2,g2) = 320
    c: DistanceY(g3,g3) = 414.663
    c: PointOnObject(g5,g3)
    c: Coincident(g5,g4)
    c: Horizontal(g5)
    c: Coincident(g6,g4)
    c: PointOnObject(g6,g1)
    c: Parallel(g6,g5)
    c: Equal(g5,g6)
    c: Diameter(g4) = 281.2
    c: DistanceY(g0,g5) = 220.831
FEATURE [PartDesign::Pad] Pad020
  Direction = (0,0,1)
  Length = 13
  Length2 = 10
  Profile = -> Sketch032
  ReferenceAxis = -> Sketch032 [N_Axis]
  Suppressed = false
  Type = 0
  expr: Length = <<bdim>>.fp_t
FEATURE [PartDesign::Body] Body021  label="front_panel"
  AllowCompound = false
  Group = -> [Sketch032,Pad020]
  Origin = -> Origin022
  Tip = -> Pad020
COMPONENT P22 — recipe-attached ("brace_bar_back_panel_e", modeled in this document).
Construction recipe (the document's own serialized feature program — sketch geometry with constraints, then the solid features built on it; lengths are millimeters unless a unit is written):

FEATURE [Sketcher::SketchObject] Sketch050
  ArcFitTolerance = 1e-06
  AttachmentSupport = -> [XY_Plane041]
  FullyConstrained = true
  MakeInternals = false
  MapMode = 5
  expr: Constraints[10] = <<bdim>>.mbbbp2_h
  expr: Constraints[9] = <<bdim>>.mbbbp2_w
  sketch-geometry (4):
    g0: LineSegment StartX=0 StartY=0 StartZ=0 EndX=30 EndY=0 EndZ=0
    g1: LineSegment StartX=30 StartY=0 StartZ=0 EndX=30 EndY=134.331 EndZ=0
    g2: LineSegment StartX=30 StartY=134.331 StartZ=0 EndX=0 EndY=134.331 EndZ=0
    g3: LineSegment StartX=0 StartY=134.331 StartZ=0 EndX=0 EndY=0 EndZ=0
  constraints (11):
    c: Coincident(g0,g1)
    c: Coincident(g1,g2)
    c: Coincident(g2,g3)
    c: Coincident(g3,g0)
    c: Horizontal(g0)
    c: Horizontal(g2)
    c: Vertical(g1)
    c: Vertical(g3)
    c: Coincident(g0,g-1)
    c: DistanceY(g3,g3) = 134.331
    c: DistanceX(g2,g2) = 30
FEATURE [PartDesign::Pad] Pad038
  Direction = (0,0,1)
  Length = 30
  Length2 = 10
  Profile = -> Sketch050
  ReferenceAxis = -> Sketch050 [N_Axis]
  Suppressed = false
  Type = 0
  expr: Length = <<bdim>>.mbbbp2_t
FEATURE [PartDesign::Body] Body040  label="middle_brace_bar_back_panel_2_model"
  AllowCompound = false
  Group = -> [Sketch050,Pad038]
  Origin = -> Origin041
  Tip = -> Pad038
COMPONENT P23 — recipe-attached ("middle brace bar fin 1", modeled in this document).
Construction recipe (the document's own serialized feature program — sketch geometry with constraints, then the solid features built on it; lengths are millimeters unless a unit is written):

FEATURE [Sketcher::SketchObject] Sketch
  ArcFitTolerance = 1e-06
  AttachmentSupport = -> [YZ_Plane028]
  FullyConstrained = true
  MakeInternals = false
  MapMode = 5
  Placement = pos=(0,0,0) rot=(0.57735,0.57735,0.57735;2.0944rad)
  expr: Constraints[10] = <<bdim>>.mbbf1_w
  expr: Constraints[9] = <<bdim>>.mbbf1_h
  sketch-geometry (4):
    g0: LineSegment StartX=0 StartY=0 StartZ=0 EndX=449.669 EndY=0 EndZ=0
    g1: LineSegment StartX=449.669 StartY=0 StartZ=0 EndX=449.669 EndY=30 EndZ=0
    g2: LineSegment StartX=449.669 StartY=30 StartZ=0 EndX=0 EndY=30 EndZ=0
    g3: LineSegment StartX=0 StartY=30 StartZ=0 EndX=0 EndY=0 EndZ=0
  constraints (11):
    c: Coincident(g0,g1)
    c: Coincident(g1,g2)
    c: Coincident(g2,g3)
    c: Coincident(g3,g0)
    c: Horizontal(g0)
    c: Horizontal(g2)
    c: Vertical(g1)
    c: Vertical(g3)
    c: Coincident(g0,g-1)
    c: DistanceY(g1,g1) = 30
    c: DistanceX(g2,g2) = 449.669
FEATURE [PartDesign::Pad] Pad026
  Direction = (1,0,0)
  Length = 30
  Length2 = 10
  Placement = pos=(0,0,0) rot=(1,1,1;2.0944rad)
  Profile = -> Sketch
  ReferenceAxis = -> Sketch [N_Axis]
  Suppressed = false
  Type = 0
  expr: Length = <<bdim>>.mbbf1_t
FEATURE [PartDesign::Body] Body027  label="middle brace bar fin 1 model"
  AllowCompound = false
  Group = -> [Sketch,Pad026]
  Origin = -> Origin028
  Tip = -> Pad026
COMPONENT P24 — recipe-attached ("middle_brace_bar_fin_1and_2_fin2", modeled in this document).
Construction recipe (the document's own serialized feature program — sketch geometry with constraints, then the solid features built on it; lengths are millimeters unless a unit is written):

FEATURE [Sketcher::SketchObject] Sketch045
  ArcFitTolerance = 1e-06
  AttachmentSupport = -> [YZ_Plane036]
  FullyConstrained = true
  MakeInternals = false
  MapMode = 5
  Placement = pos=(0,0,0) rot=(0.57735,0.57735,0.57735;2.0944rad)
  expr: Constraints[10] = <<bdim>>.mbbf12_w
  expr: Constraints[9] = <<bdim>>.mbbf12_h
  sketch-geometry (4):
    g0: LineSegment StartX=0 StartY=0 StartZ=0 EndX=30 EndY=0 EndZ=0
    g1: LineSegment StartX=30 StartY=0 StartZ=0 EndX=30 EndY=285.337 EndZ=0
    g2: LineSegment StartX=30 StartY=285.337 StartZ=0 EndX=0 EndY=285.337 EndZ=0
    g3: LineSegment StartX=0 StartY=285.337 StartZ=0 EndX=0 EndY=0 EndZ=0
  constraints (11):
    c: Coincident(g0,g1)
    c: Coincident(g1,g2)
    c: Coincident(g2,g3)
    c: Coincident(g3,g0)
    c: Horizontal(g0)
    c: Horizontal(g2)
    c: Vertical(g1)
    c: Vertical(g3)
    c: Coincident(g0,g-1)
    c: DistanceX(g2,g2) = 30
    c: DistanceY(g1,g1) = 285.337
FEATURE [PartDesign::Pad] Pad033
  Direction = (1,0,0)
  Length = 30
  Length2 = 10
  Placement = pos=(0,0,0) rot=(1,1,1;2.0944rad)
  Profile = -> Sketch045
  ReferenceAxis = -> Sketch045 [N_Axis]
  Suppressed = false
  Type = 0
  expr: Length = <<bdim>>.mbbf12_t
FEATURE [PartDesign::Body] Body035  label="middle_brace_bar_fin_1and_2"
  AllowCompound = false
  Group = -> [Sketch045,Pad033]
  Origin = -> Origin036
  Tip = -> Pad033
COMPONENT P25 — same part as P24; its construction recipe is shown at P24.
COMPONENT P26 — recipe-attached ("middle_brace_bar_fin_2", modeled in this document).
Construction recipe (the document's own serialized feature program — sketch geometry with constraints, then the solid features built on it; lengths are millimeters unless a unit is written):

FEATURE [Sketcher::SketchObject] Sketch040
  ArcFitTolerance = 1e-06
  AttachmentSupport = -> [XZ_Plane031]
  FullyConstrained = true
  MakeInternals = false
  MapMode = 5
  Placement = pos=(0,0,0) rot=(1,0,0;1.5708rad)
  expr: Constraints[10] = <<bdim>>.mbbf2_w
  expr: Constraints[9] = <<bdim>>.mbbf2_h
  sketch-geometry (4):
    g0: LineSegment StartX=0 StartY=0 StartZ=0 EndX=30 EndY=0 EndZ=0
    g1: LineSegment StartX=30 StartY=0 StartZ=0 EndX=30 EndY=505.669 EndZ=0
    g2: LineSegment StartX=30 StartY=505.669 StartZ=0 EndX=0 EndY=505.669 EndZ=0
    g3: LineSegment StartX=0 StartY=505.669 StartZ=0 EndX=0 EndY=0 EndZ=0
  constraints (11):
    c: Coincident(g0,g1)
    c: Coincident(g1,g2)
    c: Coincident(g2,g3)
    c: Coincident(g3,g0)
    c: Horizontal(g0)
    c: Horizontal(g2)
    c: Vertical(g1)
    c: Vertical(g3)
    c: Coincident(g0,g-1)
    c: DistanceX(g2,g2) = 30
    c: DistanceY(g1,g1) = 505.669
FEATURE [PartDesign::Pad] Pad028
  Direction = (0,-1,2e-16)
  Length = 30
  Length2 = 10
  Placement = pos=(0,0,0) rot=(1,0,0;1.5708rad)
  Profile = -> Sketch040
  ReferenceAxis = -> Sketch040 [N_Axis]
  Suppressed = false
  Type = 0
  expr: Length = <<bdim>>.mbbf2_t
FEATURE [PartDesign::Body] Body030  label="middle_brace_bar_fin_2_model"
  AllowCompound = false
  Group = -> [Sketch040,Pad028]
  Origin = -> Origin031
  Tip = -> Pad028
COMPONENT P27 — recipe-attached ("middle_brace_bar_side_panel_1", modeled in this document).
Construction recipe (the document's own serialized feature program — sketch geometry with constraints, then the solid features built on it; lengths are millimeters unless a unit is written):

FEATURE [Sketcher::SketchObject] Sketch044
  ArcFitTolerance = 1e-06
  AttachmentSupport = -> [XZ_Plane035]
  FullyConstrained = true
  MakeInternals = false
  MapMode = 5
  Placement = pos=(0,0,0) rot=(1,0,0;1.5708rad)
  expr: Constraints[10] = <<bdim>>.mbbsp1_w
  expr: Constraints[9] = <<bdim>>.mbbsp1_h
  sketch-geometry (4):
    g0: LineSegment StartX=0 StartY=0 StartZ=0 EndX=30 EndY=0 EndZ=0
    g1: LineSegment StartX=30 StartY=0 StartZ=0 EndX=30 EndY=614 EndZ=0
    g2: LineSegment StartX=30 StartY=614 StartZ=0 EndX=0 EndY=614 EndZ=0
    g3: LineSegment StartX=0 StartY=614 StartZ=0 EndX=0 EndY=0 EndZ=0
  constraints (11):
    c: Coincident(g0,g1)
    c: Coincident(g1,g2)
    c: Coincident(g2,g3)
    c: Coincident(g3,g0)
    c: Horizontal(g0)
    c: Horizontal(g2)
    c: Vertical(g1)
    c: Vertical(g3)
    c: Coincident(g0,g-1)
    c: DistanceX(g2,g2) = 30
    c: DistanceY(g1,g1) = 614
FEATURE [PartDesign::Pad] Pad032
  AlongSketchNormal = false
  Direction = (0,-1,2e-16)
  Length = 30
  Length2 = 10
  Placement = pos=(0,0,0) rot=(1,0,0;1.5708rad)
  Profile = -> Sketch044
  ReferenceAxis = -> Sketch044 [N_Axis]
  Suppressed = false
  Type = 0
  expr: Length = <<bdim>>.mbbsp1_t
FEATURE [PartDesign::Body] Body034  label="middle_brace_bar_side_panel_1_model"
  AllowCompound = false
  Group = -> [Sketch044,Pad032]
  Origin = -> Origin035
  Tip = -> Pad032
COMPONENT P28 — recipe-attached ("middle_brace_bar_side_panel_2", modeled in this document).
Construction recipe (the document's own serialized feature program — sketch geometry with constraints, then the solid features built on it; lengths are millimeters unless a unit is written):

FEATURE [Sketcher::SketchObject] Sketch041
  ArcFitTolerance = 1e-06
  AttachmentSupport = -> [XZ_Plane032]
  FullyConstrained = true
  MakeInternals = false
  MapMode = 5
  Placement = pos=(0,0,0) rot=(1,0,0;1.5708rad)
  expr: Constraints[10] = <<bdim>>.mbbsp2_w
  expr: Constraints[9] = <<bdim>>.mbbsp2_h
  sketch-geometry (4):
    g0: LineSegment StartX=0 StartY=0 StartZ=0 EndX=30 EndY=0 EndZ=0
    g1: LineSegment StartX=30 StartY=0 StartZ=0 EndX=30 EndY=657 EndZ=0
    g2: LineSegment StartX=30 StartY=657 StartZ=0 EndX=0 EndY=657 EndZ=0
    g3: LineSegment StartX=0 StartY=657 StartZ=0 EndX=0 EndY=0 EndZ=0
  constraints (11):
    c: Coincident(g0,g1)
    c: Coincident(g1,g2)
    c: Coincident(g2,g3)
    c: Coincident(g3,g0)
    c: Horizontal(g0)
    c: Horizontal(g2)
    c: Vertical(g1)
    c: Vertical(g3)
    c: Coincident(g0,g-1)
    c: DistanceX(g2,g2) = 30
    c: DistanceY(g1,g1) = 657
FEATURE [PartDesign::Pad] Pad029
  Direction = (0,-1,2e-16)
  Length = 30
  Length2 = 10
  Placement = pos=(0,0,0) rot=(1,0,0;1.5708rad)
  Profile = -> Sketch041
  ReferenceAxis = -> Sketch041 [N_Axis]
  Suppressed = false
  Type = 0
  expr: Length = <<bdim>>.mbbsp2_t
FEATURE [PartDesign::Body] Body031  label="middle_brace_bar_side_panel_003"
  AllowCompound = false
  Group = -> [Sketch041,Pad029]
  Origin = -> Origin032
  Tip = -> Pad029
COMPONENT P29 — recipe-attached ("side_panel_1", modeled in this document).
Construction recipe (the document's own serialized feature program — sketch geometry with constraints, then the solid features built on it; lengths are millimeters unless a unit is written):

FEATURE [Sketcher::SketchObject] Sketch020
  ArcFitTolerance = 1e-06
  AttachmentSupport = -> [XZ_Plane010]
  FullyConstrained = true
  MakeInternals = false
  MapMode = 5
  Placement = pos=(0,0,0) rot=(1,0,0;1.5708rad)
  expr: Constraints[10] = <<bdim>>.sp_h
  expr: Constraints[9] = <<bdim>>.sp_w
  sketch-geometry (4):
    g0: LineSegment StartX=0 StartY=0 StartZ=0 EndX=674 EndY=0 EndZ=0
    g1: LineSegment StartX=674 StartY=0 StartZ=0 EndX=674 EndY=320 EndZ=0
    g2: LineSegment StartX=674 StartY=320 StartZ=0 EndX=0 EndY=320 EndZ=0
    g3: LineSegment StartX=0 StartY=320 StartZ=0 EndX=0 EndY=0 EndZ=0
  constraints (11):
    c: Coincident(g0,g1)
    c: Coincident(g1,g2)
    c: Coincident(g2,g3)
    c: Coincident(g3,g0)
    c: Horizontal(g0)
    c: Horizontal(g2)
    c: Vertical(g1)
    c: Vertical(g3)
    c: Coincident(g0,g-1)
    c: DistanceY(g3,g3) = 320
    c: DistanceX(g0,g0) = 674
FEATURE [PartDesign::Pad] Pad008
  Direction = (0,-1,2e-16)
  Length = 13
  Length2 = 10
  Placement = pos=(0,0,0) rot=(1,0,0;1.5708rad)
  Profile = -> Sketch020
  ReferenceAxis = -> Sketch020 [N_Axis]
  Suppressed = false
  Type = 0
  expr: Length = <<bdim>>.sp_thick
FEATURE [PartDesign::Body] Body009  label="side_panel_001"
  AllowCompound = false
  Group = -> [Sketch020,Pad008]
  Origin = -> Origin010
  Tip = -> Pad008
COMPONENT P30 — recipe-attached ("side_panel_1_bar_a", modeled in this document).
Construction recipe (the document's own serialized feature program — sketch geometry with constraints, then the solid features built on it; lengths are millimeters unless a unit is written):

FEATURE [Sketcher::SketchObject] Sketch021
  ArcFitTolerance = 1e-06
  AttachmentSupport = -> [XZ_Plane011]
  FullyConstrained = true
  MakeInternals = false
  MapMode = 5
  Placement = pos=(0,0,0) rot=(1,0,0;1.5708rad)
  expr: Constraints[10] = <<bdim>>.spb_h
  expr: Constraints[9] = <<bdim>>.spb_w
  sketch-geometry (4):
    g0: LineSegment StartX=0 StartY=0 StartZ=0 EndX=674 EndY=0 EndZ=0
    g1: LineSegment StartX=674 StartY=0 StartZ=0 EndX=674 EndY=30 EndZ=0
    g2: LineSegment StartX=674 StartY=30 StartZ=0 EndX=0 EndY=30 EndZ=0
    g3: LineSegment StartX=0 StartY=30 StartZ=0 EndX=0 EndY=0 EndZ=0
  constraints (11):
    c: Coincident(g0,g1)
    c: Coincident(g1,g2)
    c: Coincident(g2,g3)
    c: Coincident(g3,g0)
    c: Horizontal(g0)
    c: Horizontal(g2)
    c: Vertical(g1)
    c: Vertical(g3)
    c: Coincident(g0,g-1)
    c: DistanceX(g2,g2) = 674
    c: DistanceY(g3,g3) = 30
FEATURE [PartDesign::Pad] Pad009
  Direction = (0,-1,2e-16)
  Length = 30
  Length2 = 10
  Placement = pos=(0,0,0) rot=(1,0,0;1.5708rad)
  Profile = -> Sketch021
  ReferenceAxis = -> Sketch021 [N_Axis]
  Suppressed = false
  Type = 0
  expr: Length = <<bdim>>.spb_h
FEATURE [PartDesign::Body] Body010  label="side_panel_001_bar_001"
  AllowCompound = false
  Group = -> [Sketch021,Pad009]
  Origin = -> Origin011
  Tip = -> Pad009
COMPONENT P31 — recipe-attached ("side_panel_1_bar_b", modeled in this document).
Construction recipe (the document's own serialized feature program — sketch geometry with constraints, then the solid features built on it; lengths are millimeters unless a unit is written):

FEATURE [Sketcher::SketchObject] Sketch022
  ArcFitTolerance = 1e-06
  AttachmentSupport = -> [XZ_Plane012]
  FullyConstrained = true
  MakeInternals = false
  MapMode = 5
  Placement = pos=(0,0,0) rot=(1,0,0;1.5708rad)
  expr: Constraints[10] = <<bdim>>.spb_h
  expr: Constraints[9] = <<bdim>>.spb_w
  sketch-geometry (4):
    g0: LineSegment StartX=0 StartY=0 StartZ=0 EndX=674 EndY=0 EndZ=0
    g1: LineSegment StartX=674 StartY=0 StartZ=0 EndX=674 EndY=30 EndZ=0
    g2: LineSegment StartX=674 StartY=30 StartZ=0 EndX=0 EndY=30 EndZ=0
    g3: LineSegment StartX=0 StartY=30 StartZ=0 EndX=0 EndY=0 EndZ=0
  constraints (11):
    c: Coincident(g0,g1)
    c: Coincident(g1,g2)
    c: Coincident(g2,g3)
    c: Coincident(g3,g0)
    c: Horizontal(g0)
    c: Horizontal(g2)
    c: Vertical(g1)
    c: Vertical(g3)
    c: Coincident(g0,g-1)
    c: DistanceX(g2,g2) = 674
    c: DistanceY(g3,g3) = 30
FEATURE [PartDesign::Pad] Pad010
  Direction = (0,-1,2e-16)
  Length = 30
  Length2 = 10
  Placement = pos=(0,0,0) rot=(1,0,0;1.5708rad)
  Profile = -> Sketch022
  ReferenceAxis = -> Sketch022 [N_Axis]
  Suppressed = false
  Type = 0
  expr: Length = <<bdim>>.spb_h
FEATURE [PartDesign::Body] Body011  label="side_panel_001_bar_002"
  AllowCompound = false
  Group = -> [Sketch022,Pad010]
  Origin = -> Origin012
  Tip = -> Pad010
COMPONENT P32 — recipe-attached ("side_panel_1_bar_c", modeled in this document).
Construction recipe (the document's own serialized feature program — sketch geometry with constraints, then the solid features built on it; lengths are millimeters unless a unit is written):

FEATURE [Sketcher::SketchObject] Sketch023
  ArcFitTolerance = 1e-06
  AttachmentSupport = -> [XZ_Plane013]
  FullyConstrained = true
  MakeInternals = false
  MapMode = 5
  Placement = pos=(0,0,0) rot=(1,0,0;1.5708rad)
  expr: Constraints[10] = <<bdim>>.spbb_w
  expr: Constraints[9] = <<bdim>>.spbb_h
  sketch-geometry (4):
    g0: LineSegment StartX=0 StartY=0 StartZ=0 EndX=30 EndY=0 EndZ=0
    g1: LineSegment StartX=30 StartY=0 StartZ=0 EndX=30 EndY=260 EndZ=0
    g2: LineSegment StartX=30 StartY=260 StartZ=0 EndX=0 EndY=260 EndZ=0
    g3: LineSegment StartX=0 StartY=260 StartZ=0 EndX=0 EndY=0 EndZ=0
  constraints (11):
    c: Coincident(g0,g1)
    c: Coincident(g1,g2)
    c: Coincident(g2,g3)
    c: Coincident(g3,g0)
    c: Horizontal(g0)
    c: Horizontal(g2)
    c: Vertical(g1)
    c: Vertical(g3)
    c: Coincident(g0,g-1)
    c: DistanceX(g2,g2) = 30
    c: DistanceY(g3,g3) = 260
FEATURE [PartDesign::Pad] Pad011
  Direction = (0,-1,2e-16)
  Length = 30
  Length2 = 10
  Placement = pos=(0,0,0) rot=(1,0,0;1.5708rad)
  Profile = -> Sketch023
  ReferenceAxis = -> Sketch023 [N_Axis]
  Suppressed = false
  Type = 0
  expr: Length = <<bdim>>.spb_h
FEATURE [PartDesign::Body] Body012  label="side_panel_001_bar_003"
  AllowCompound = false
  Group = -> [Sketch023,Pad011]
  Origin = -> Origin013
  Tip = -> Pad011
COMPONENT P33 — recipe-attached ("side_panel_1_bar_d", modeled in this document).
Construction recipe (the document's own serialized feature program — sketch geometry with constraints, then the solid features built on it; lengths are millimeters unless a unit is written):

FEATURE [Sketcher::SketchObject] Sketch024
  ArcFitTolerance = 1e-06
  AttachmentSupport = -> [XZ_Plane014]
  FullyConstrained = true
  MakeInternals = false
  MapMode = 5
  Placement = pos=(0,0,0) rot=(1,0,0;1.5708rad)
  expr: Constraints[10] = <<bdim>>.spbb_w
  expr: Constraints[9] = <<bdim>>.spbb_h
  sketch-geometry (4):
    g0: LineSegment StartX=0 StartY=0 StartZ=0 EndX=30 EndY=0 EndZ=0
    g1: LineSegment StartX=30 StartY=0 StartZ=0 EndX=30 EndY=260 EndZ=0
    g2: LineSegment StartX=30 StartY=260 StartZ=0 EndX=0 EndY=260 EndZ=0
    g3: LineSegment StartX=0 StartY=260 StartZ=0 EndX=0 EndY=0 EndZ=0
  constraints (11):
    c: Coincident(g0,g1)
    c: Coincident(g1,g2)
    c: Coincident(g2,g3)
    c: Coincident(g3,g0)
    c: Horizontal(g0)
    c: Horizontal(g2)
    c: Vertical(g1)
    c: Vertical(g3)
    c: Coincident(g0,g-1)
    c: DistanceX(g2,g2) = 30
    c: DistanceY(g3,g3) = 260
FEATURE [PartDesign::Pad] Pad012
  Direction = (0,-1,2e-16)
  Length = 30
  Length2 = 10
  Placement = pos=(0,0,0) rot=(1,0,0;1.5708rad)
  Profile = -> Sketch024
  ReferenceAxis = -> Sketch024 [N_Axis]
  Suppressed = false
  Type = 0
  expr: Length = <<bdim>>.spb_h
FEATURE [PartDesign::Body] Body013  label="side_panel_001_bar_004"
  AllowCompound = false
  Group = -> [Sketch024,Pad012]
  Origin = -> Origin014
  Tip = -> Pad012
COMPONENT P34 — same part as P33; its construction recipe is shown at P33.
COMPONENT P35 — same part as P33; its construction recipe is shown at P33.
COMPONENT P36 — recipe-attached ("side_panel_2", modeled in this document).
Construction recipe (the document's own serialized feature program — sketch geometry with constraints, then the solid features built on it; lengths are millimeters unless a unit is written):

FEATURE [Sketcher::SketchObject] Sketch025
  ArcFitTolerance = 1e-06
  AttachmentSupport = -> [XZ_Plane015]
  FullyConstrained = true
  MakeInternals = false
  MapMode = 5
  Placement = pos=(0,0,0) rot=(1,0,0;1.5708rad)
  expr: Constraints[10] = <<bdim>>.sp2_h
  expr: Constraints[9] = <<bdim>>.sp2_w
  sketch-geometry (4):
    g0: LineSegment StartX=0 StartY=0 StartZ=0 EndX=687 EndY=0 EndZ=0
    g1: LineSegment StartX=687 StartY=0 StartZ=0 EndX=687 EndY=320 EndZ=0
    g2: LineSegment StartX=687 StartY=320 StartZ=0 EndX=0 EndY=320 EndZ=0
    g3: LineSegment StartX=0 StartY=320 StartZ=0 EndX=0 EndY=0 EndZ=0
  constraints (11):
    c: Coincident(g0,g1)
    c: Coincident(g1,g2)
    c: Coincident(g2,g3)
    c: Coincident(g3,g0)
    c: Horizontal(g0)
    c: Horizontal(g2)
    c: Vertical(g1)
    c: Vertical(g3)
    c: Coincident(g0,g-1)
    c: DistanceY(g3,g3) = 320
    c: DistanceX(g0,g0) = 687
FEATURE [PartDesign::Pad] Pad013
  Direction = (0,-1,2e-16)
  Length = 13
  Length2 = 10
  Placement = pos=(0,0,0) rot=(1,0,0;1.5708rad)
  Profile = -> Sketch025
  ReferenceAxis = -> Sketch025 [N_Axis]
  Suppressed = false
  Type = 0
  expr: Length = <<bdim>>.sp_thick
FEATURE [PartDesign::Body] Body014  label="side_panel_002"
  AllowCompound = false
  Group = -> [Sketch025,Pad013]
  Origin = -> Origin015
  Tip = -> Pad013
COMPONENT P37 — recipe-attached ("side_panel_2_bar_a", modeled in this document).
Construction recipe (the document's own serialized feature program — sketch geometry with constraints, then the solid features built on it; lengths are millimeters unless a unit is written):

FEATURE [Sketcher::SketchObject] Sketch026
  ArcFitTolerance = 1e-06
  AttachmentSupport = -> [XZ_Plane016]
  FullyConstrained = true
  MakeInternals = false
  MapMode = 5
  Placement = pos=(0,0,0) rot=(1,0,0;1.5708rad)
  expr: Constraints[10] = <<bdim>>.sp2b1_h
  expr: Constraints[9] = <<bdim>>.sp2b1_w
  sketch-geometry (4):
    g0: LineSegment StartX=0 StartY=0 StartZ=0 EndX=687 EndY=0 EndZ=0
    g1: LineSegment StartX=687 StartY=0 StartZ=0 EndX=687 EndY=30 EndZ=0
    g2: LineSegment StartX=687 StartY=30 StartZ=0 EndX=0 EndY=30 EndZ=0
    g3: LineSegment StartX=0 StartY=30 StartZ=0 EndX=0 EndY=0 EndZ=0
  constraints (11):
    c: Coincident(g0,g1)
    c: Coincident(g1,g2)
    c: Coincident(g2,g3)
    c: Coincident(g3,g0)
    c: Horizontal(g0)
    c: Horizontal(g2)
    c: Vertical(g1)
    c: Vertical(g3)
    c: Coincident(g0,g-1)
    c: DistanceX(g2,g2) = 687
    c: DistanceY(g3,g3) = 30
FEATURE [PartDesign::Pad] Pad014
  Direction = (0,-1,2e-16)
  Length = 30
  Length2 = 10
  Placement = pos=(0,0,0) rot=(1,0,0;1.5708rad)
  Profile = -> Sketch026
  ReferenceAxis = -> Sketch026 [N_Axis]
  Suppressed = false
  Type = 0
  expr: Length = <<bdim>>.spb_h
FEATURE [PartDesign::Body] Body015  label="side_panel_002_bar_001"
  AllowCompound = false
  Group = -> [Sketch026,Pad014]
  Origin = -> Origin016
  Tip = -> Pad014
COMPONENT P38 — recipe-attached ("side_panel_2_bar_b", modeled in this document).
Construction recipe (the document's own serialized feature program — sketch geometry with constraints, then the solid features built on it; lengths are millimeters unless a unit is written):

FEATURE [Sketcher::SketchObject] Sketch027
  ArcFitTolerance = 1e-06
  AttachmentSupport = -> [XZ_Plane017]
  FullyConstrained = true
  MakeInternals = false
  MapMode = 5
  Placement = pos=(0,0,0) rot=(1,0,0;1.5708rad)
  expr: Constraints[10] = <<bdim>>.sp2b1_h
  expr: Constraints[9] = <<bdim>>.sp2b1_w
  sketch-geometry (4):
    g0: LineSegment StartX=0 StartY=0 StartZ=0 EndX=687 EndY=0 EndZ=0
    g1: LineSegment StartX=687 StartY=0 StartZ=0 EndX=687 EndY=30 EndZ=0
    g2: LineSegment StartX=687 StartY=30 StartZ=0 EndX=0 EndY=30 EndZ=0
    g3: LineSegment StartX=0 StartY=30 StartZ=0 EndX=0 EndY=0 EndZ=0
  constraints (11):
    c: Coincident(g0,g1)
    c: Coincident(g1,g2)
    c: Coincident(g2,g3)
    c: Coincident(g3,g0)
    c: Horizontal(g0)
    c: Horizontal(g2)
    c: Vertical(g1)
    c: Vertical(g3)
    c: Coincident(g0,g-1)
    c: DistanceX(g2,g2) = 687
    c: DistanceY(g3,g3) = 30
FEATURE [PartDesign::Pad] Pad015
  Direction = (0,-1,2e-16)
  Length = 30
  Length2 = 10
  Placement = pos=(0,0,0) rot=(1,0,0;1.5708rad)
  Profile = -> Sketch027
  ReferenceAxis = -> Sketch027 [N_Axis]
  Suppressed = false
  Type = 0
  expr: Length = <<bdim>>.spb_h
FEATURE [PartDesign::Body] Body016  label="side_panel_002_bar_002"
  AllowCompound = false
  Group = -> [Sketch027,Pad015]
  Origin = -> Origin017
  Tip = -> Pad015
COMPONENT P39 — recipe-attached ("side_panel_2_bar_c", modeled in this document).
Construction recipe (the document's own serialized feature program — sketch geometry with constraints, then the solid features built on it; lengths are millimeters unless a unit is written):

FEATURE [Sketcher::SketchObject] Sketch029
  ArcFitTolerance = 1e-06
  AttachmentSupport = -> [XZ_Plane019]
  FullyConstrained = true
  MakeInternals = false
  MapMode = 5
  Placement = pos=(0,0,0) rot=(1,0,0;1.5708rad)
  expr: Constraints[10] = <<bdim>>.sp2b2_w
  expr: Constraints[9] = <<bdim>>.sp2b2_h
  sketch-geometry (4):
    g0: LineSegment StartX=0 StartY=0 StartZ=0 EndX=30 EndY=0 EndZ=0
    g1: LineSegment StartX=30 StartY=0 StartZ=0 EndX=30 EndY=260 EndZ=0
    g2: LineSegment StartX=30 StartY=260 StartZ=0 EndX=0 EndY=260 EndZ=0
    g3: LineSegment StartX=0 StartY=260 StartZ=0 EndX=0 EndY=0 EndZ=0
  constraints (11):
    c: Coincident(g0,g1)
    c: Coincident(g1,g2)
    c: Coincident(g2,g3)
    c: Coincident(g3,g0)
    c: Horizontal(g0)
    c: Horizontal(g2)
    c: Vertical(g1)
    c: Vertical(g3)
    c: Coincident(g0,g-1)
    c: DistanceX(g2,g2) = 30
    c: DistanceY(g3,g3) = 260
FEATURE [PartDesign::Pad] Pad017
  Direction = (0,-1,2e-16)
  Length = 30
  Length2 = 10
  Placement = pos=(0,0,0) rot=(1,0,0;1.5708rad)
  Profile = -> Sketch029
  ReferenceAxis = -> Sketch029 [N_Axis]
  Suppressed = false
  Type = 0
  expr: Length = <<bdim>>.spb_h
FEATURE [PartDesign::Body] Body018  label="side_panel_002_bar_004"
  AllowCompound = false
  Group = -> [Sketch029,Pad017]
  Origin = -> Origin019
  Tip = -> Pad017
COMPONENT P40 — recipe-attached ("top_panel001", modeled in this document).
Construction recipe (the document's own serialized feature program — sketch geometry with constraints, then the solid features built on it; lengths are millimeters unless a unit is written):

FEATURE [Sketcher::SketchObject] Sketch018
  ArcFitTolerance = 1e-06
  AttachmentSupport = -> [YZ_Plane008]
  FullyConstrained = true
  MakeInternals = false
  MapMode = 5
  Placement = pos=(0,0,0) rot=(0.57735,0.57735,0.57735;2.0944rad)
  expr: Constraints[10] = <<bdim>>.tp_h
  expr: Constraints[9] = <<bdim>>.tp_w
  sketch-geometry (4):
    g0: LineSegment StartX=0 StartY=0 StartZ=0 EndX=635 EndY=0 EndZ=0
    g1: LineSegment StartX=635 StartY=0 StartZ=0 EndX=635 EndY=700 EndZ=0
    g2: LineSegment StartX=635 StartY=700 StartZ=0 EndX=0 EndY=700 EndZ=0
    g3: LineSegment StartX=0 StartY=700 StartZ=0 EndX=0 EndY=0 EndZ=0
  constraints (11):
    c: Coincident(g0,g1)
    c: Coincident(g1,g2)
    c: Coincident(g2,g3)
    c: Coincident(g3,g0)
    c: Horizontal(g0)
    c: Horizontal(g2)
    c: Vertical(g1)
    c: Vertical(g3)
    c: Coincident(g0,g-1)
    c: DistanceX(g0,g0) = 635
    c: DistanceY(g3,g3) = 700
FEATURE [PartDesign::Pad] Pad007
  Direction = (1,0,0)
  Length = 13
  Length2 = 10
  Placement = pos=(0,0,0) rot=(1,1,1;2.0944rad)
  Profile = -> Sketch018
  ReferenceAxis = -> Sketch018 [N_Axis]
  Suppressed = false
  Type = 0
  expr: Length = <<bdim>>.tp_t
FEATURE [PartDesign::Body] Body007  label="top_panel"
  AllowCompound = false
  Group = -> [Sketch018,Pad007]
  Origin = -> Origin008
  Tip = -> Pad007
PROVENANCE & LICENSES
A FreeCAD (.FCStd) document from a public repository crawl; recipes are the document's own serialized feature recipes (and, for linked parts, companion documents' recipes).
License: as declared in the source repository (recorded in the dataset sidecar).
